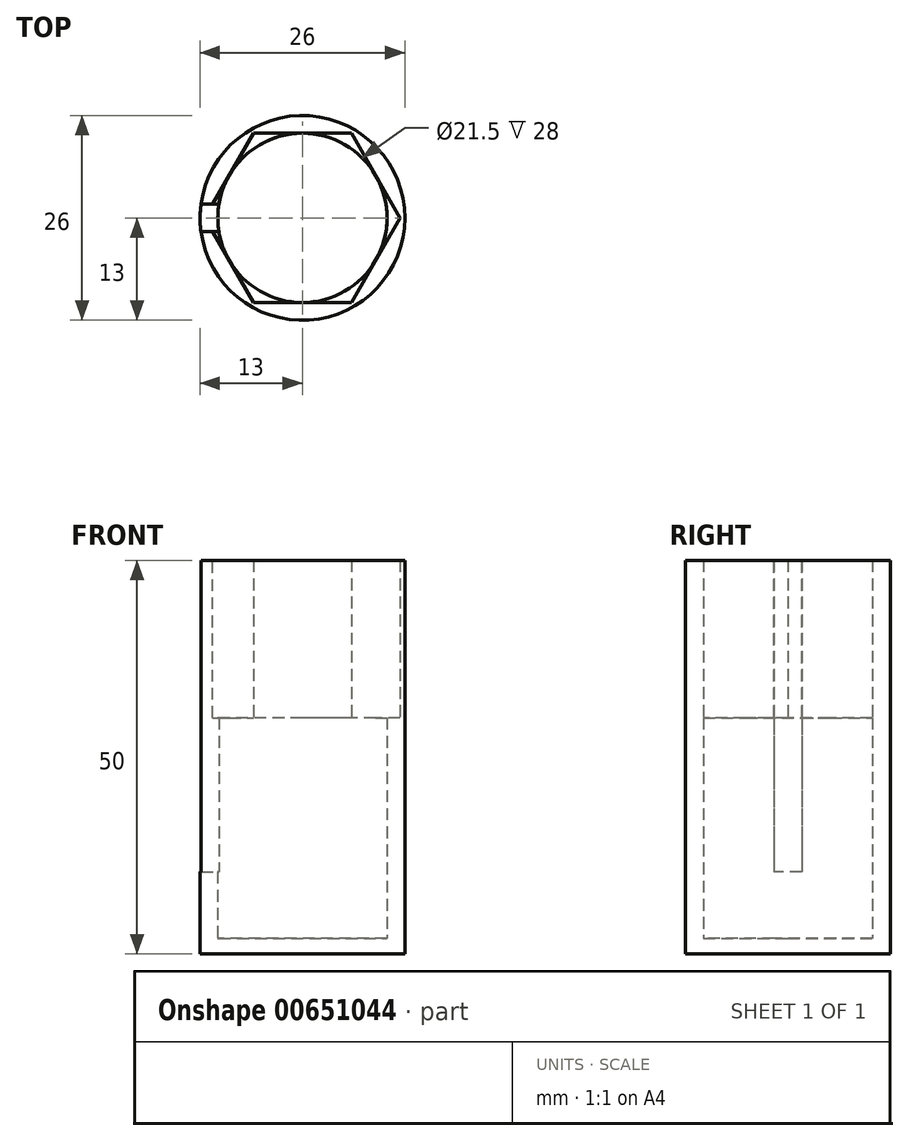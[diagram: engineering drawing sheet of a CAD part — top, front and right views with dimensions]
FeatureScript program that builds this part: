
annotation { "Feature Type Name" : "Feature", "Feature Type Description" : "" }
export const myFeature = defineFeature(function(context is Context, id is Id, definition is map)
    precondition{}
    {
        {
            var Q0;
            Q0=qCreatedBy(makeId("Top.planeOp"),FACE);
            var sketch = newSketch(context, id + "F0", { "sketchPlane" : qUnion([Q0])});
            skCircle(sketch, "E0", {"center": v(0, 0) * mm, "radius": 13 * mm});
            skCircle(sketch, "E1.cCircle", {"center": v(0, 0) * mm, "radius": 10.75 * mm});
            skLineSegment(sketch, "E1.0", {"start": v(6.2, -10.75) * mm, "end": v(-6.2, -10.75) * mm});
            skLineSegment(sketch, "E1.1", {"start": v(-6.2, -10.75) * mm, "end": v(-12.41, 0) * mm});
            skLineSegment(sketch, "E1.2", {"start": v(-12.41, 0) * mm, "end": v(-6.2, 10.75) * mm});
            skLineSegment(sketch, "E1.3", {"start": v(-6.2, 10.75) * mm, "end": v(6.2, 10.75) * mm});
            skLineSegment(sketch, "E1.4", {"start": v(6.2, 10.75) * mm, "end": v(12.41, 0) * mm});
            skLineSegment(sketch, "E1.5", {"start": v(12.41, 0) * mm, "end": v(6.2, -10.75) * mm});
            skPoint(sketch, "E1.0.midPoint", {"position": v(0, -10.75) * mm});
            skSolve(sketch);
        }
        {
            var Q0;
            Q0=makeQuery(id+"F0.imprint","IMPRINT",FACE,{"disambiguationData":[TD([[makeQuery(id+"F0.imprint","IMPRINT",EDGE,{"derivedFrom":sQuery(id+"F0.wireOp",EDGE,"E0")}),1.0]])]});
            extrude(context, id + "F1", {"entities" : qUnion([Q0]), "depth" : 50 * mm, "offsetDistance" : 25 * mm});
        }
        {
            var Q0;
            Q0=makeQuery(id+"F0.imprint","IMPRINT",FACE,{"disambiguationData":[TD([[makeQuery(id+"F0.imprint","IMPRINT",EDGE,{"derivedFrom":sQuery(id+"F0.wireOp",EDGE,"E1.0")}),-1.0]])]});
            var Q1;
            {var subQ0=sQuery(id+"F0.wireOp",EDGE,"E1.cCircle");var subQ4=makeQuery(id+"F0.imprint","INTERSECT",VERTEX,{"derivedFrom":[subQ0,sQuery(id+"F0.wireOp",EDGE,"E1.3")]});Q1=makeQuery(id+"F0.imprint","IMPRINT",FACE,{"disambiguationData":[TD([[makeQuery(id+"F0.imprint","IMPRINT",EDGE,{"disambiguationData":[TD([[subQ4,1.0]])],"derivedFrom":subQ0}),1.0]])]});}
            var Q2;
            {var subQ0=sQuery(id+"F0.wireOp",EDGE,"E1.3");var subQ1=sQuery(id+"F0.wireOp",EDGE,"E1.cCircle");var subQ2=makeQuery(id+"F0.imprint","INTERSECT",VERTEX,{"derivedFrom":[subQ1,subQ0]});Q2=makeQuery(id+"F0.imprint","IMPRINT",FACE,{"disambiguationData":[TD([[makeQuery(id+"F0.imprint","IMPRINT",EDGE,{"disambiguationData":[TD([[subQ2,-1.0]])],"derivedFrom":subQ1}),-1.0]])]});}
            var Q3;
            {var subQ0=sQuery(id+"F0.wireOp",EDGE,"E1.2");var subQ1=sQuery(id+"F0.wireOp",EDGE,"E1.cCircle");var subQ2=makeQuery(id+"F0.imprint","INTERSECT",VERTEX,{"derivedFrom":[subQ1,subQ0]});Q3=makeQuery(id+"F0.imprint","IMPRINT",FACE,{"disambiguationData":[TD([[makeQuery(id+"F0.imprint","IMPRINT",EDGE,{"disambiguationData":[TD([[subQ2,-1.0]])],"derivedFrom":subQ1}),-1.0]])]});}
            var Q4;
            {var subQ0=sQuery(id+"F0.wireOp",EDGE,"E1.3");var subQ1=sQuery(id+"F0.wireOp",EDGE,"E1.cCircle");var subQ2=makeQuery(id+"F0.imprint","INTERSECT",VERTEX,{"derivedFrom":[subQ1,subQ0]});Q4=makeQuery(id+"F0.imprint","IMPRINT",FACE,{"disambiguationData":[TD([[makeQuery(id+"F0.imprint","IMPRINT",EDGE,{"disambiguationData":[TD([[subQ2,1.0]])],"derivedFrom":subQ1}),-1.0]])]});}
            var Q5;
            {var subQ0=sQuery(id+"F0.wireOp",EDGE,"E1.4");var subQ1=sQuery(id+"F0.wireOp",EDGE,"E1.cCircle");var subQ2=makeQuery(id+"F0.imprint","INTERSECT",VERTEX,{"derivedFrom":[subQ1,subQ0]});Q5=makeQuery(id+"F0.imprint","IMPRINT",FACE,{"disambiguationData":[TD([[makeQuery(id+"F0.imprint","IMPRINT",EDGE,{"disambiguationData":[TD([[subQ2,1.0]])],"derivedFrom":subQ1}),-1.0]])]});}
            extrude(context, id + "F2", {"entities" : qUnion([Q0, Q1, Q2, Q3, Q4, Q5]), "operationType" : NewBodyOperationType.ADD, "depth" : 2 * mm, "offsetDistance" : 25 * mm});
        }
        {
            var Q0;
            Q0=qCreatedBy(makeId("Right.planeOp"),FACE);
            var sketch = newSketch(context, id + "F3", { "sketchPlane" : qUnion([Q0])});
            skLineSegment(sketch, "E2.bottom", {"start": v(1.76, 50.44) * mm, "end": v(-1.74, 50.44) * mm});
            skLineSegment(sketch, "E2.top", {"start": v(1.76, 10.44) * mm, "end": v(-1.74, 10.44) * mm});
            skLineSegment(sketch, "E2.left", {"start": v(1.76, 50.44) * mm, "end": v(1.76, 10.44) * mm});
            skLineSegment(sketch, "E2.right", {"start": v(-1.74, 50.44) * mm, "end": v(-1.74, 10.44) * mm});
            skSolve(sketch);
        }
        {
            var Q0;
            {var subQ0=sQuery(id+"F0.wireOp",EDGE,"E1.3");var subQ1=sQuery(id+"F0.wireOp",EDGE,"E1.cCircle");var subQ2=makeQuery(id+"F0.imprint","INTERSECT",VERTEX,{"derivedFrom":[subQ1,subQ0]});Q0=makeQuery(id+"F0.imprint","IMPRINT",FACE,{"disambiguationData":[TD([[makeQuery(id+"F0.imprint","IMPRINT",EDGE,{"disambiguationData":[TD([[subQ2,1.0]])],"derivedFrom":subQ1}),-1.0]])]});}
            var Q1;
            {var subQ0=sQuery(id+"F0.wireOp",EDGE,"E1.3");var subQ1=sQuery(id+"F0.wireOp",EDGE,"E1.cCircle");var subQ2=makeQuery(id+"F0.imprint","INTERSECT",VERTEX,{"derivedFrom":[subQ1,subQ0]});Q1=makeQuery(id+"F0.imprint","IMPRINT",FACE,{"disambiguationData":[TD([[makeQuery(id+"F0.imprint","IMPRINT",EDGE,{"disambiguationData":[TD([[subQ2,-1.0]])],"derivedFrom":subQ1}),-1.0]])]});}
            var Q2;
            {var subQ0=sQuery(id+"F0.wireOp",EDGE,"E1.2");var subQ1=sQuery(id+"F0.wireOp",EDGE,"E1.cCircle");var subQ2=makeQuery(id+"F0.imprint","INTERSECT",VERTEX,{"derivedFrom":[subQ1,subQ0]});Q2=makeQuery(id+"F0.imprint","IMPRINT",FACE,{"disambiguationData":[TD([[makeQuery(id+"F0.imprint","IMPRINT",EDGE,{"disambiguationData":[TD([[subQ2,-1.0]])],"derivedFrom":subQ1}),-1.0]])]});}
            var Q3;
            {var subQ0=sQuery(id+"F0.wireOp",EDGE,"E1.1");var subQ1=sQuery(id+"F0.wireOp",EDGE,"E1.cCircle");var subQ2=makeQuery(id+"F0.imprint","INTERSECT",VERTEX,{"derivedFrom":[subQ1,subQ0]});Q3=makeQuery(id+"F0.imprint","IMPRINT",FACE,{"disambiguationData":[TD([[makeQuery(id+"F0.imprint","IMPRINT",EDGE,{"disambiguationData":[TD([[subQ2,-1.0]])],"derivedFrom":subQ1}),-1.0]])]});}
            var Q4;
            {var subQ0=sQuery(id+"F0.wireOp",EDGE,"E1.0");var subQ1=sQuery(id+"F0.wireOp",EDGE,"E1.cCircle");var subQ2=makeQuery(id+"F0.imprint","INTERSECT",VERTEX,{"derivedFrom":[subQ1,subQ0]});Q4=makeQuery(id+"F0.imprint","IMPRINT",FACE,{"disambiguationData":[TD([[makeQuery(id+"F0.imprint","IMPRINT",EDGE,{"disambiguationData":[TD([[subQ2,-1.0]])],"derivedFrom":subQ1}),-1.0]])]});}
            var Q5;
            {var subQ0=sQuery(id+"F0.wireOp",EDGE,"E1.4");var subQ1=sQuery(id+"F0.wireOp",EDGE,"E1.cCircle");var subQ2=makeQuery(id+"F0.imprint","INTERSECT",VERTEX,{"derivedFrom":[subQ1,subQ0]});Q5=makeQuery(id+"F0.imprint","IMPRINT",FACE,{"disambiguationData":[TD([[makeQuery(id+"F0.imprint","IMPRINT",EDGE,{"disambiguationData":[TD([[subQ2,1.0]])],"derivedFrom":subQ1}),-1.0]])]});}
            extrude(context, id + "F4", {"entities" : qUnion([Q0, Q1, Q2, Q3, Q4, Q5]), "operationType" : NewBodyOperationType.ADD, "depth" : 30 * mm, "offsetDistance" : 25 * mm});
        }
        {
            var Q0;
            Q0=makeQuery(id+"F3.imprint","IMPRINT",FACE,{"disambiguationData":[TD([[makeQuery(id+"F3.imprint","IMPRINT",EDGE,{"derivedFrom":sQuery(id+"F3.wireOp",EDGE,"E2.bottom")}),1.0]])]});
            extrude(context, id + "F5", {"entities" : qUnion([Q0]), "operationType" : NewBodyOperationType.REMOVE, "oppositeDirection" : true, "depth" : 25 * mm, "offsetDistance" : 25 * mm});
        }
    });
